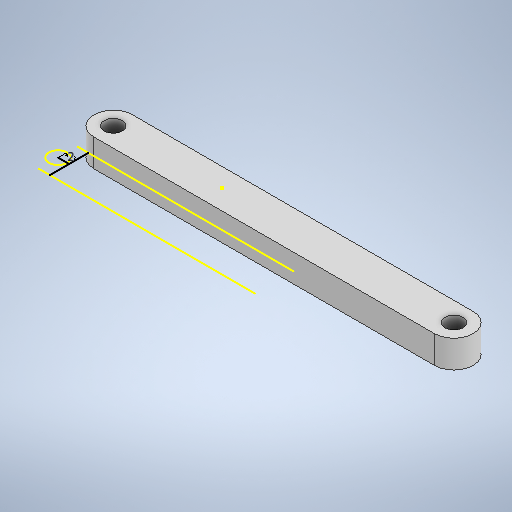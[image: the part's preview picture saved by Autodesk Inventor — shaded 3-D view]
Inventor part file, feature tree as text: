
AUTODESK INVENTOR PART (.ipt)
format: ipt  version: 2025.1 (Build 291241020, 241B)  size: 331,264 bytes
history: native  units: mm
features: sketch x7, extrude x4, move_body x4, boolean_combine x4, split x3, other x1, fillet x1, plane x1, imported_body x1
ambient origin geometry x8: Origin, YZ Plane, XZ Plane, XY Plane, X Axis, Y Axis, Z Axis, Center Point
bodies: Solid1 (feature_tree), Solid2 (feature_tree), Solid3 (feature_tree), Solid4 (feature_tree), Solid5 (feature_tree), Solid6 (feature_tree), Solid7 (feature_tree), Solid8 (feature_tree)
feature tree (26):
  other  "Repaired Geometry1"
  extrude  "Extrusion1"  Depth=7.0mm
  fillet  "Fillet1"  Radius=3.3mm
  move_body  "Move Body1"
  split  "Split1"
  move_body  "Move Body2"
  boolean_combine  "Combine1"
  sketch  "Sketch4"  dims[d5=3.5mm d6=5.0mm d7=0.0mm]
  plane  "Work Plane1"
  split  "Split2"
  split  "Split3"
  move_body  "Move Body3"
  move_body  "Move Body4"
  sketch  "Sketch5"  dims[d8=3.5mm d9=0.0mm d10=0.0mm d11=10.0mm]
  sketch  "Sketch6"  dims[d12=-0.1mm d13=0.0mm d14=0.0mm]
  extrude  "Extrusion2"  Depth=3.5mm
  extrude  "Extrusion3"  Depth=5.0mm TaperAngle=0.0deg
  boolean_combine  "Combine2"
  boolean_combine  "Combine3"
  sketch  "Sketch7"  dims[d15=2.0mm]
  boolean_combine  "Combine4"
  extrude  "Extrusion4"  Depth=10.0mm TaperAngle=0.0deg
  sketch  "Sketch1"  dims[d0=7.0mm d1=39.4mm d2=3.3mm]
  imported_body  "Base1"
  sketch  "Sketch2"  dims[d3=3.3mm d4=3.5mm]
  sketch  "Sketch8"  dims[d16=90.0deg d17=22.5mm d18=0.0mm d19=0.0mm d20=10.7mm d21=0.0mm d22=0.0mm d23=10.0mm d24=0.0mm d25=10.0mm d26=0.0mm d27=10.0mm d28=0.0mm]
